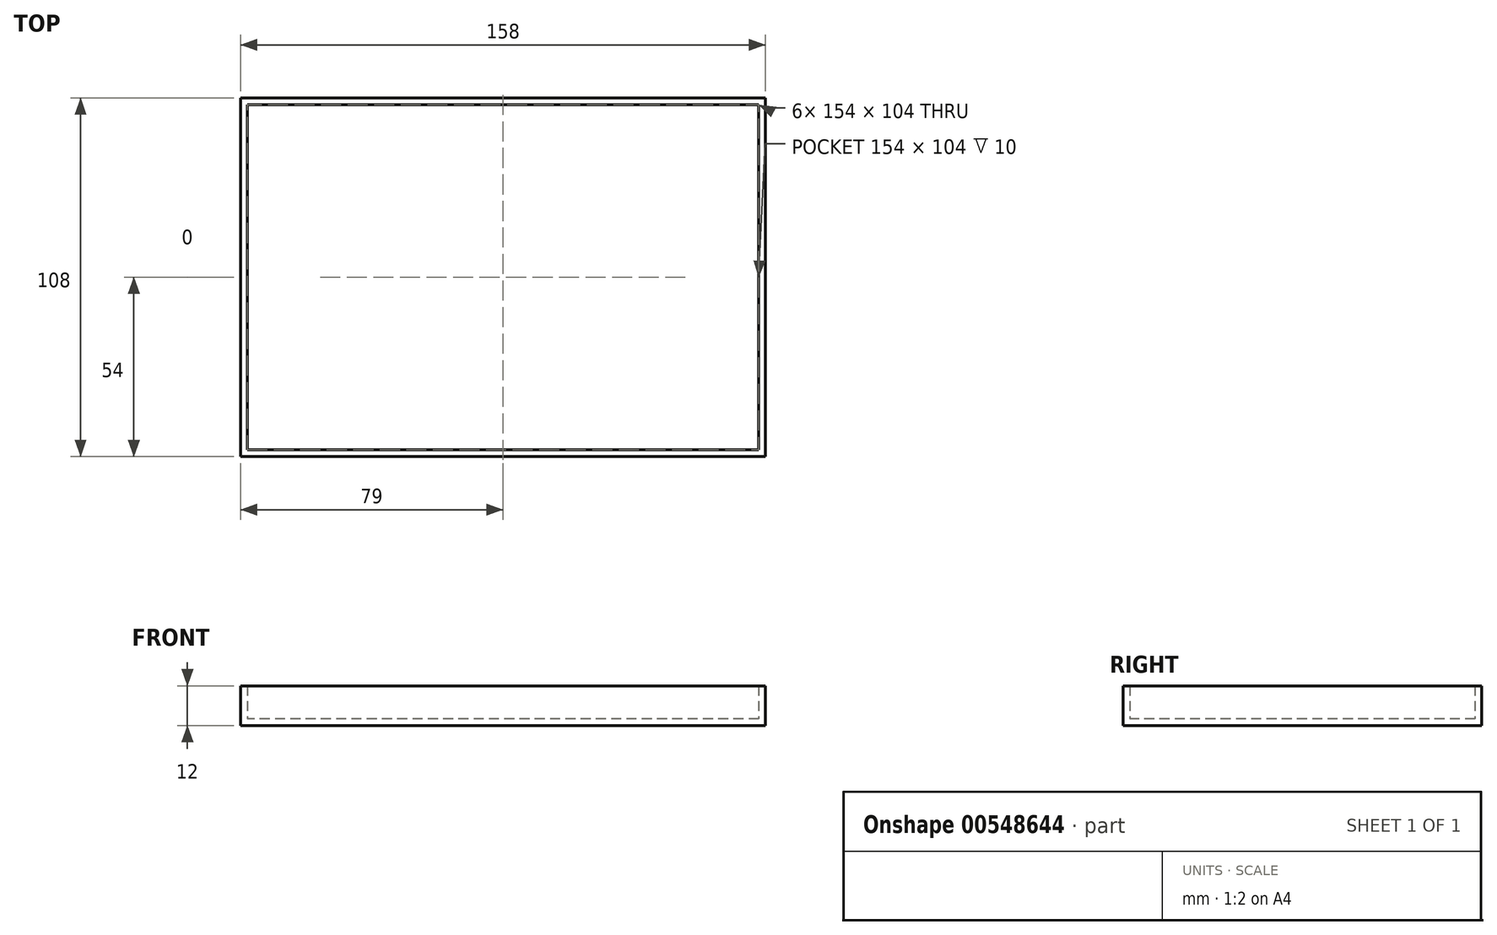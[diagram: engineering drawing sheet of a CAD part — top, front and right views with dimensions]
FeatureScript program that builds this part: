
annotation { "Feature Type Name" : "Feature", "Feature Type Description" : "" }
export const myFeature = defineFeature(function(context is Context, id is Id, definition is map)
    precondition{}
    {
        {
            var Q0;
            Q0=qCreatedBy(makeId("Top.planeOp"),FACE);
            var sketch = newSketch(context, id + "F0", { "sketchPlane" : qUnion([Q0])});
            skLineSegment(sketch, "E0.bottom", {"start": v(77, 52) * mm, "end": v(-77, 52) * mm});
            skLineSegment(sketch, "E0.top", {"start": v(77, -52) * mm, "end": v(-77, -52) * mm});
            skLineSegment(sketch, "E0.left", {"start": v(77, 52) * mm, "end": v(77, -52) * mm});
            skLineSegment(sketch, "E0.right", {"start": v(-77, 52) * mm, "end": v(-77, -52) * mm});
            skPoint(sketch, "E0.middle", {"position": v(0, 0) * mm});
            skSolve(sketch);
        }
        {
            var Q0;
            Q0=makeQuery(id+"F0.imprint","IMPRINT",FACE,{"disambiguationData":[TD([[makeQuery(id+"F0.imprint","IMPRINT",EDGE,{"derivedFrom":sQuery(id+"F0.wireOp",EDGE,"E0.bottom")}),1.0]])]});
            extrude(context, id + "F1", {"entities" : qUnion([Q0]), "depth" : 10 * mm, "offsetDistance" : 25 * mm});
        }
        {
            var Q0;
            Q0=makeQuery(id+"F1.opExtrude","CAP_FACE",FACE,{"disambiguationData":[OSD([sQuery(id+"F0.wireOp",EDGE,"E0.bottom"),sQuery(id+"F0.wireOp",EDGE,"E0.top"),sQuery(id+"F0.wireOp",EDGE,"E0.left"),sQuery(id+"F0.wireOp",EDGE,"E0.right")])],"isStart":false});
            shell(context, id + "F2", {"entities" : qUnion([Q0]), "thickness" : 2 * mm, "oppositeDirection" : true});
        }
    });
